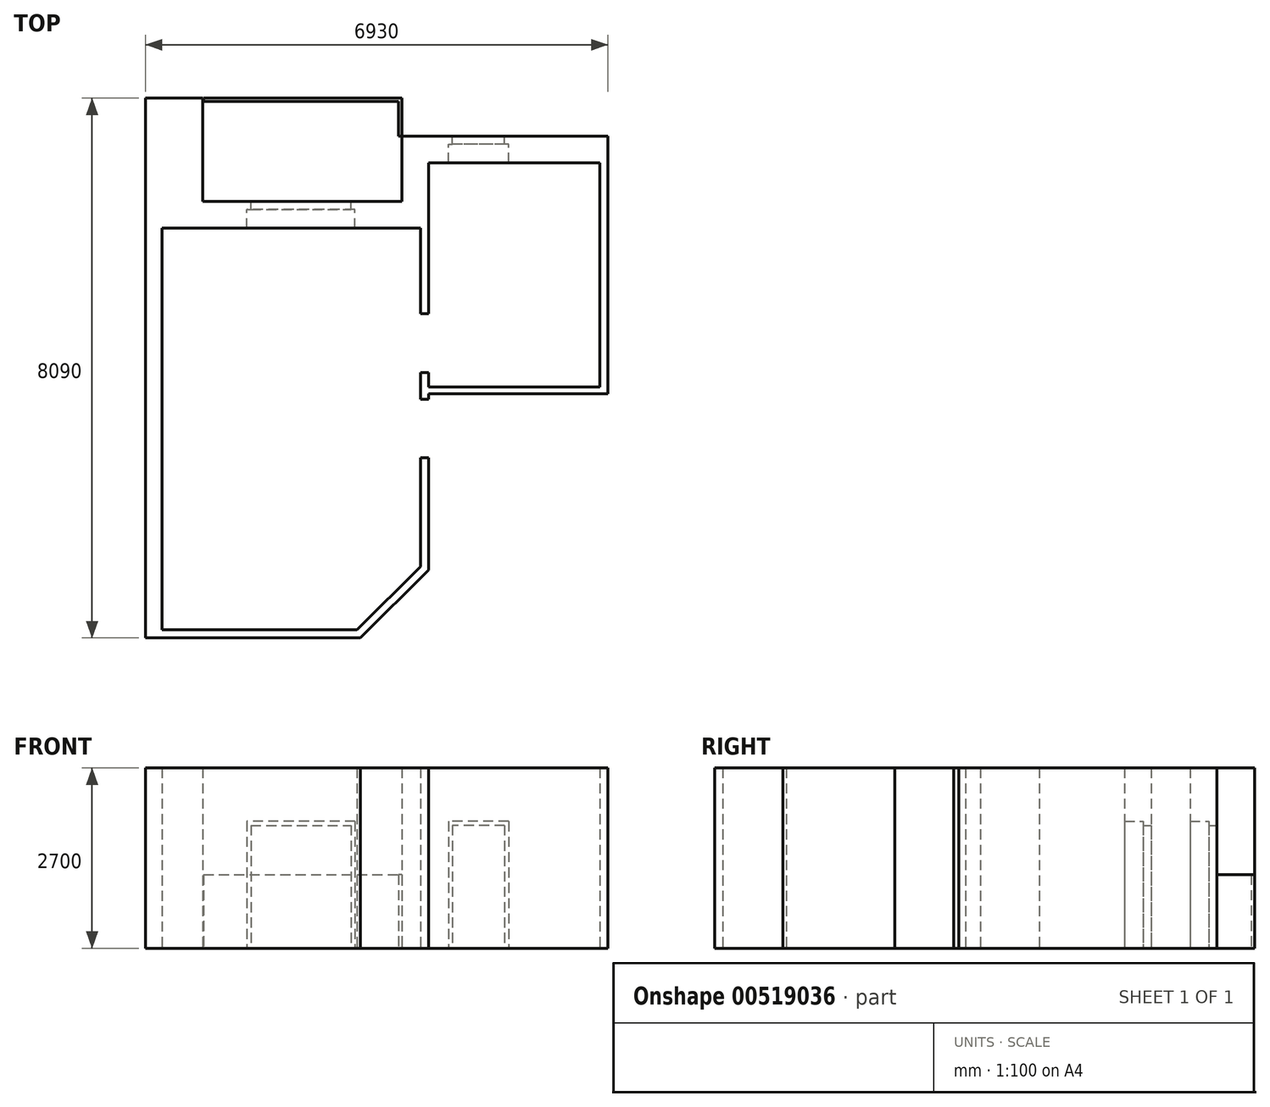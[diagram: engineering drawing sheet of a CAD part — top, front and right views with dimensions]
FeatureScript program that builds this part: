
annotation { "Feature Type Name" : "Feature", "Feature Type Description" : "" }
export const myFeature = defineFeature(function(context is Context, id is Id, definition is map)
    precondition{}
    {
        {
            var Q0;
            Q0=qCreatedBy(makeId("Top.planeOp"),FACE);
            var sketch = newSketch(context, id + "F0", { "sketchPlane" : qUnion([Q0])});
            skLineSegment(sketch, "E0", {"start": v(0, 0) * mm, "end": v(0, -6020) * mm, "construction": true});
            skLineSegment(sketch, "E1", {"start": v(0, -6020) * mm, "end": v(2920, -6020) * mm, "construction": true});
            skLineSegment(sketch, "E2", {"start": v(2920, -6020) * mm, "end": v(3870, -5070) * mm, "construction": true});
            skLineSegment(sketch, "E3", {"start": v(3870, -5070) * mm, "end": v(3870, 0) * mm, "construction": true});
            skLineSegment(sketch, "E4", {"start": v(3870, 0) * mm, "end": v(0, 0) * mm, "construction": true});
            skLineSegment(sketch, "E5.bottom", {"start": v(3990, 980) * mm, "end": v(6560, 980) * mm, "construction": true});
            skLineSegment(sketch, "E5.top", {"start": v(3990, -2380) * mm, "end": v(6560, -2380) * mm, "construction": true});
            skLineSegment(sketch, "E5.left", {"start": v(3990, 980) * mm, "end": v(3990, -2380) * mm, "construction": true});
            skLineSegment(sketch, "E5.right", {"start": v(6560, 980) * mm, "end": v(6560, -2380) * mm, "construction": true});
            skSolve(sketch);
        }
        {
            var Q0;
            Q0=qCreatedBy(makeId("Top.planeOp"),FACE);
            var sketch = newSketch(context, id + "F1", { "sketchPlane" : qUnion([Q0])});
            skLineSegment(sketch, "E6.0", {"start": v(0, 0) * mm, "end": v(0, -6020) * mm});
            skLineSegment(sketch, "E6.1", {"start": v(0, -6020) * mm, "end": v(2920, -6020) * mm});
            skLineSegment(sketch, "E6.2", {"start": v(2920, -6020) * mm, "end": v(3870, -5070) * mm});
            skLineSegment(sketch, "E6.3", {"start": v(3990, -2380) * mm, "end": v(6560, -2380) * mm});
            skLineSegment(sketch, "E6.4", {"start": v(6560, 980) * mm, "end": v(6560, -2380) * mm});
            skLineSegment(sketch, "E7", {"start": v(0, 0) * mm, "end": v(1270, 0) * mm});
            skLineSegment(sketch, "E8", {"start": v(1270, 0) * mm, "end": v(1270, 280) * mm});
            skLineSegment(sketch, "E9", {"start": v(1270, 280) * mm, "end": v(1330, 280) * mm});
            skLineSegment(sketch, "E10", {"start": v(1330, 280) * mm, "end": v(1330, 400) * mm});
            skLineSegment(sketch, "E11", {"start": v(2080, 0) * mm, "end": v(2080, 400) * mm, "construction": true});
            skLineSegment(sketch, "E12.MirrorCS", {"start": v(2890, 0) * mm, "end": v(2890, 280) * mm});
            skLineSegment(sketch, "E13.MirrorCS", {"start": v(2890, 280) * mm, "end": v(2830, 280) * mm});
            skLineSegment(sketch, "E14.MirrorCS", {"start": v(2830, 280) * mm, "end": v(2830, 400) * mm});
            skLineSegment(sketch, "E15", {"start": v(2890, 0) * mm, "end": v(3870, 0) * mm});
            skLineSegment(sketch, "E16", {"start": v(2830, 400) * mm, "end": v(3590, 400) * mm});
            skLineSegment(sketch, "E17", {"start": v(3590, 400) * mm, "end": v(3590, 1380) * mm});
            skLineSegment(sketch, "E18", {"start": v(3590, 1380) * mm, "end": v(4350, 1380) * mm});
            skLineSegment(sketch, "E19", {"start": v(3590, 1950) * mm, "end": v(3590, 1380) * mm});
            skLineSegment(sketch, "E20", {"start": v(3870, 0) * mm, "end": v(3870, -1280) * mm});
            skLineSegment(sketch, "E21", {"start": v(3870, -1280) * mm, "end": v(3990, -1280) * mm});
            skLineSegment(sketch, "E22", {"start": v(3990, -1280) * mm, "end": v(3990, 980) * mm});
            skLineSegment(sketch, "E23", {"start": v(3990, 980) * mm, "end": v(4290, 980) * mm});
            skLineSegment(sketch, "E24", {"start": v(4290, 980) * mm, "end": v(4290, 1260) * mm});
            skLineSegment(sketch, "E25", {"start": v(4290, 1260) * mm, "end": v(4350, 1260) * mm});
            skLineSegment(sketch, "E26", {"start": v(4350, 1260) * mm, "end": v(4350, 1380) * mm});
            skLineSegment(sketch, "E27", {"start": v(3870, -2560) * mm, "end": v(3990, -2560) * mm});
            skLineSegment(sketch, "E28", {"start": v(3870, -2560) * mm, "end": v(3870, -2160) * mm});
            skLineSegment(sketch, "E29", {"start": v(3870, -2160) * mm, "end": v(3990, -2160) * mm});
            skLineSegment(sketch, "E30", {"start": v(3990, -2160) * mm, "end": v(3990, -2380) * mm});
            skLineSegment(sketch, "E31", {"start": v(3990, -2560) * mm, "end": v(3990, -2482.77) * mm});
            skLineSegment(sketch, "E32", {"start": v(4740, 983.64) * mm, "end": v(4740, 1358.16) * mm, "construction": true});
            skLineSegment(sketch, "E33.MirrorCS", {"start": v(5130, 1260) * mm, "end": v(5130, 1380) * mm});
            skLineSegment(sketch, "E34.MirrorCS", {"start": v(5190, 980) * mm, "end": v(5190, 1260) * mm});
            skLineSegment(sketch, "E35.MirrorCS", {"start": v(5190, 1260) * mm, "end": v(5130, 1260) * mm});
            skLineSegment(sketch, "E36", {"start": v(5190, 980) * mm, "end": v(6560, 980) * mm});
            skLineSegment(sketch, "E37", {"start": v(5130, 1380) * mm, "end": v(6680, 1380) * mm});
            skLineSegment(sketch, "E38", {"start": v(6680, 1380) * mm, "end": v(6680, -2482.77) * mm});
            skLineSegment(sketch, "E39", {"start": v(3990, -2482.77) * mm, "end": v(6680, -2482.77) * mm});
            skLineSegment(sketch, "E40", {"start": v(3870, -5070) * mm, "end": v(3870, -3440) * mm});
            skLineSegment(sketch, "E41", {"start": v(3870, -3440) * mm, "end": v(3990, -3440) * mm});
            skLineSegment(sketch, "E42.0", {"start": v(3990, -5119.7) * mm, "end": v(3990, -3440) * mm});
            skLineSegment(sketch, "E42.1", {"start": v(2969.7, -6140) * mm, "end": v(3990, -5119.7) * mm});
            skLineSegment(sketch, "E42.2", {"start": v(-250, -6140) * mm, "end": v(2969.7, -6140) * mm});
            skLineSegment(sketch, "E43.0", {"start": v(-250, 1950) * mm, "end": v(-250, -6140) * mm});
            skLineSegment(sketch, "E44", {"start": v(-250, 1950) * mm, "end": v(610, 1950) * mm});
            skLineSegment(sketch, "E45", {"start": v(610, 1950) * mm, "end": v(610, 400) * mm});
            skLineSegment(sketch, "E46", {"start": v(610, 400) * mm, "end": v(1330, 400) * mm});
            skLineSegment(sketch, "E47.0", {"start": v(3540, 1900) * mm, "end": v(3540, 1380) * mm});
            skLineSegment(sketch, "E47.1", {"start": v(620, 1900) * mm, "end": v(3540, 1900) * mm});
            skLineSegment(sketch, "E48", {"start": v(3590, 1380) * mm, "end": v(3540, 1380) * mm});
            skLineSegment(sketch, "E49", {"start": v(620, 1900) * mm, "end": v(620, 1950) * mm});
            skLineSegment(sketch, "E50", {"start": v(620, 1950) * mm, "end": v(3590, 1950) * mm});
            skSolve(sketch);
        }
        {
            var Q0;
            Q0=makeQuery(id+"F1.imprint","IMPRINT",FACE,{"disambiguationData":[TD([[makeQuery(id+"F1.imprint","IMPRINT",EDGE,{"derivedFrom":sQuery(id+"F1.wireOp",EDGE,"E6.0")}),-1.0]])]});
            var Q1;
            Q1=makeQuery(id+"F1.imprint","IMPRINT",FACE,{"disambiguationData":[TD([[makeQuery(id+"F1.imprint","IMPRINT",EDGE,{"derivedFrom":sQuery(id+"F1.wireOp",EDGE,"E12.MirrorCS")}),-1.0]])]});
            var Q2;
            Q2=makeQuery(id+"F1.imprint","IMPRINT",FACE,{"disambiguationData":[TD([[makeQuery(id+"F1.imprint","IMPRINT",EDGE,{"derivedFrom":sQuery(id+"F1.wireOp",EDGE,"E6.3")}),-1.0]])]});
            extrude(context, id + "F2", {"entities" : qUnion([Q0, Q1, Q2]), "depth" : 2700 * mm, "offsetDistance" : 25 * mm});
        }
        {
            var Q0;
            Q0=makeQuery(id+"F1.imprint","IMPRINT",FACE,{"disambiguationData":[TD([[makeQuery(id+"F1.imprint","IMPRINT",EDGE,{"derivedFrom":sQuery(id+"F1.wireOp",EDGE,"E19")}),-1.0]])]});
            extrude(context, id + "F3", {"entities" : qUnion([Q0]), "depth" : 1100 * mm, "offsetDistance" : 25 * mm});
        }
        {
            var Q0;
            Q0=makeQuery(id+"F2.opExtrude","CAP_FACE",FACE,{"disambiguationData":[OSD([sQuery(id+"F1.wireOp",EDGE,"E6.0"),sQuery(id+"F1.wireOp",EDGE,"E6.1"),sQuery(id+"F1.wireOp",EDGE,"E6.2"),sQuery(id+"F1.wireOp",EDGE,"E7"),sQuery(id+"F1.wireOp",EDGE,"E8"),sQuery(id+"F1.wireOp",EDGE,"E9"),sQuery(id+"F1.wireOp",EDGE,"E10"),sQuery(id+"F1.wireOp",EDGE,"E40"),sQuery(id+"F1.wireOp",EDGE,"E41"),sQuery(id+"F1.wireOp",EDGE,"E42.0"),sQuery(id+"F1.wireOp",EDGE,"E42.1"),sQuery(id+"F1.wireOp",EDGE,"E42.2"),sQuery(id+"F1.wireOp",EDGE,"E43.0"),sQuery(id+"F1.wireOp",EDGE,"E44"),sQuery(id+"F1.wireOp",EDGE,"E45"),sQuery(id+"F1.wireOp",EDGE,"E46")])],"isStart":false});
            var sketch = newSketch(context, id + "F4", { "sketchPlane" : qUnion([Q0])});
            skLineSegment(sketch, "E51.0", {"start": v(1330, 280) * mm, "end": v(1330, 400) * mm});
            skLineSegment(sketch, "E51.1", {"start": v(1270, 280) * mm, "end": v(1330, 280) * mm});
            skLineSegment(sketch, "E51.2", {"start": v(1270, 0) * mm, "end": v(1270, 280) * mm});
            skLineSegment(sketch, "E51.3", {"start": v(2890, 0) * mm, "end": v(2890, 280) * mm});
            skLineSegment(sketch, "E51.4", {"start": v(2890, 280) * mm, "end": v(2830, 280) * mm});
            skLineSegment(sketch, "E51.5", {"start": v(2830, 280) * mm, "end": v(2830, 400) * mm});
            skLineSegment(sketch, "E52", {"start": v(1330, 400) * mm, "end": v(2830, 400) * mm});
            skLineSegment(sketch, "E53", {"start": v(1270, 0) * mm, "end": v(2890, 0) * mm});
            skLineSegment(sketch, "E54.0", {"start": v(4350, 1260) * mm, "end": v(4350, 1380) * mm});
            skLineSegment(sketch, "E54.1", {"start": v(4290, 1260) * mm, "end": v(4350, 1260) * mm});
            skLineSegment(sketch, "E54.2", {"start": v(4290, 980) * mm, "end": v(4290, 1260) * mm});
            skLineSegment(sketch, "E54.3", {"start": v(5130, 1260) * mm, "end": v(5130, 1380) * mm});
            skLineSegment(sketch, "E54.4", {"start": v(5190, 1260) * mm, "end": v(5130, 1260) * mm});
            skLineSegment(sketch, "E54.5", {"start": v(5190, 980) * mm, "end": v(5190, 1260) * mm});
            skLineSegment(sketch, "E55", {"start": v(5130, 1380) * mm, "end": v(4350, 1380) * mm});
            skLineSegment(sketch, "E56", {"start": v(4290, 980) * mm, "end": v(5190, 980) * mm});
            skSolve(sketch);
        }
        {
            var Q0;
            Q0 = qSketchRegion(id + "F4", true);
            extrude(context, id + "F5", {"entities" : qUnion([Q0]), "operationType" : NewBodyOperationType.ADD, "oppositeDirection" : true, "depth" : 800 * mm, "offsetDistance" : 25 * mm});
        }
        {
            var Q0;
            Q0=makeQuery(id+"F5.opExtrude","CAP_FACE",FACE,{"disambiguationData":[OSD([sQuery(id+"F4.wireOp",EDGE,"E51.0"),sQuery(id+"F4.wireOp",EDGE,"E51.1"),sQuery(id+"F4.wireOp",EDGE,"E51.2"),sQuery(id+"F4.wireOp",EDGE,"E51.3"),sQuery(id+"F4.wireOp",EDGE,"E51.4"),sQuery(id+"F4.wireOp",EDGE,"E51.5"),sQuery(id+"F4.wireOp",EDGE,"E52"),sQuery(id+"F4.wireOp",EDGE,"E53")])],"isStart":false});
            var sketch = newSketch(context, id + "F6", { "sketchPlane" : qUnion([Q0])});
            skLineSegment(sketch, "E57.bottom", {"start": v(1330, -280) * mm, "end": v(2830, -280) * mm});
            skLineSegment(sketch, "E57.top", {"start": v(1330, -400) * mm, "end": v(2830, -400) * mm});
            skLineSegment(sketch, "E57.left", {"start": v(1330, -280) * mm, "end": v(1330, -400) * mm});
            skLineSegment(sketch, "E57.right", {"start": v(2830, -280) * mm, "end": v(2830, -400) * mm});
            skLineSegment(sketch, "E58.bottom", {"start": v(5130, -1260) * mm, "end": v(4350, -1260) * mm});
            skLineSegment(sketch, "E58.top", {"start": v(5130, -1380) * mm, "end": v(4350, -1380) * mm});
            skLineSegment(sketch, "E58.left", {"start": v(5130, -1260) * mm, "end": v(5130, -1380) * mm});
            skLineSegment(sketch, "E58.right", {"start": v(4350, -1260) * mm, "end": v(4350, -1380) * mm});
            skSolve(sketch);
        }
        {
            var Q0;
            Q0 = qSketchRegion(id + "F6", true);
            extrude(context, id + "F7", {"entities" : qUnion([Q0]), "operationType" : NewBodyOperationType.ADD, "depth" : 60 * mm, "offsetDistance" : 25 * mm});
        }
    });
